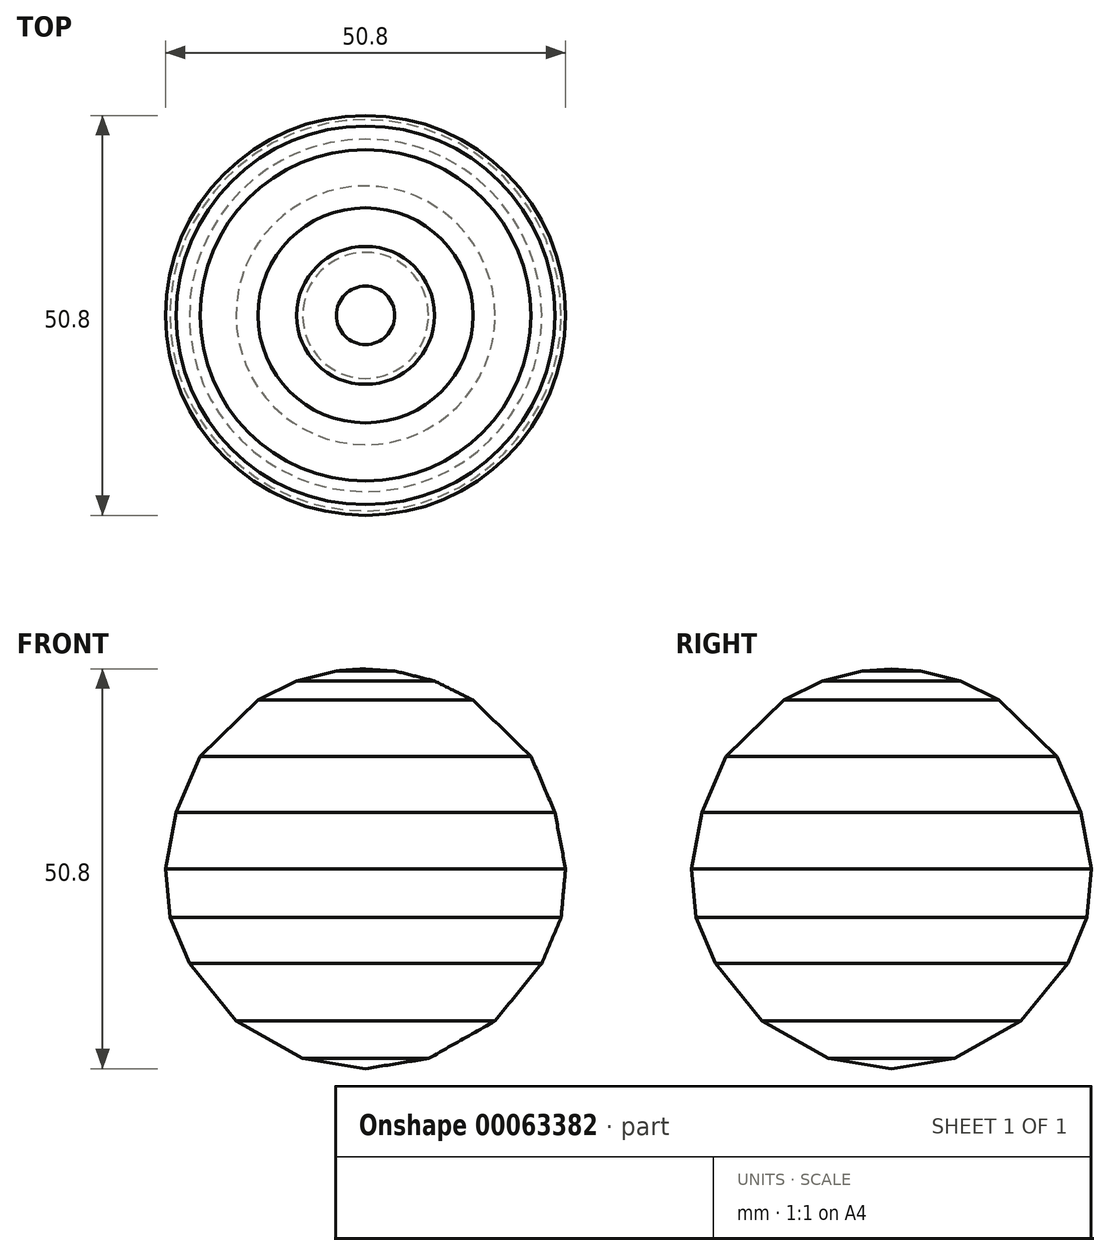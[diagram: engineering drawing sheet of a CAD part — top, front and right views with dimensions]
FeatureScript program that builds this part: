
annotation { "Feature Type Name" : "Feature", "Feature Type Description" : "" }
export const myFeature = defineFeature(function(context is Context, id is Id, definition is map)
    precondition{}
    {
        {
            var Q0;
            Q0=qCreatedBy(makeId("Right.planeOp"),FACE);
            var sketch = newSketch(context, id + "F0", { "sketchPlane" : qUnion([Q0])});
            skLineSegment(sketch, "E0", {"start": v(0, 62.48) * mm, "end": v(0, -41.16) * mm, "construction": true});
            skLineSegment(sketch, "E1", {"start": v(0, 25.4) * mm, "end": v(0, -25.4) * mm});
            skLineSegment(sketch, "E2", {"start": v(13.66, 21.42) * mm, "end": v(21.03, 14.25) * mm});
            skLineSegment(sketch, "E3", {"start": v(22.38, -12) * mm, "end": v(16.44, -19.36) * mm});
            skLineSegment(sketch, "E4", {"start": v(16.44, -19.36) * mm, "end": v(8, -24.1) * mm});
            skLineSegment(sketch, "E5", {"start": v(8, -24.1) * mm, "end": v(0, -25.4) * mm});
            skLineSegment(sketch, "E6", {"start": v(13.66, 21.42) * mm, "end": v(8.76, 23.84) * mm});
            skLineSegment(sketch, "E7", {"start": v(8.76, 23.84) * mm, "end": v(3.71, 25.13) * mm});
            skLineSegment(sketch, "E8", {"start": v(3.71, 25.13) * mm, "end": v(0, 25.4) * mm});
            skLineSegment(sketch, "E9", {"start": v(21.03, 14.25) * mm, "end": v(24.06, 7.12) * mm});
            skPoint(sketch, "E9.endSnap0", {"position": v(23.21, 7.12) * mm});
            skLineSegment(sketch, "E10", {"start": v(24.06, 7.12) * mm, "end": v(25.4, 0) * mm});
            skLineSegment(sketch, "E11", {"start": v(25.4, 0) * mm, "end": v(24.85, -6.2) * mm});
            skLineSegment(sketch, "E12", {"start": v(24.85, -6.2) * mm, "end": v(22.38, -12) * mm});
            skSolve(sketch);
        }
        {
            var Q0;
            Q0=makeQuery(id+"F0.imprint","IMPRINT",FACE,{"disambiguationData":[TD([[makeQuery(id+"F0.imprint","IMPRINT",EDGE,{"derivedFrom":sQuery(id+"F0.wireOp",EDGE,"E1")}),1.0]])]});
            var Q1;
            Q1=sQuery(id+"F0.wireOp",EDGE,"E0");
            revolve(context, id + "F1", {"entities" : qUnion([Q0]), "axis" : qUnion([Q1]), "revolveType" : RevolveType.FULL});
        }
    });
